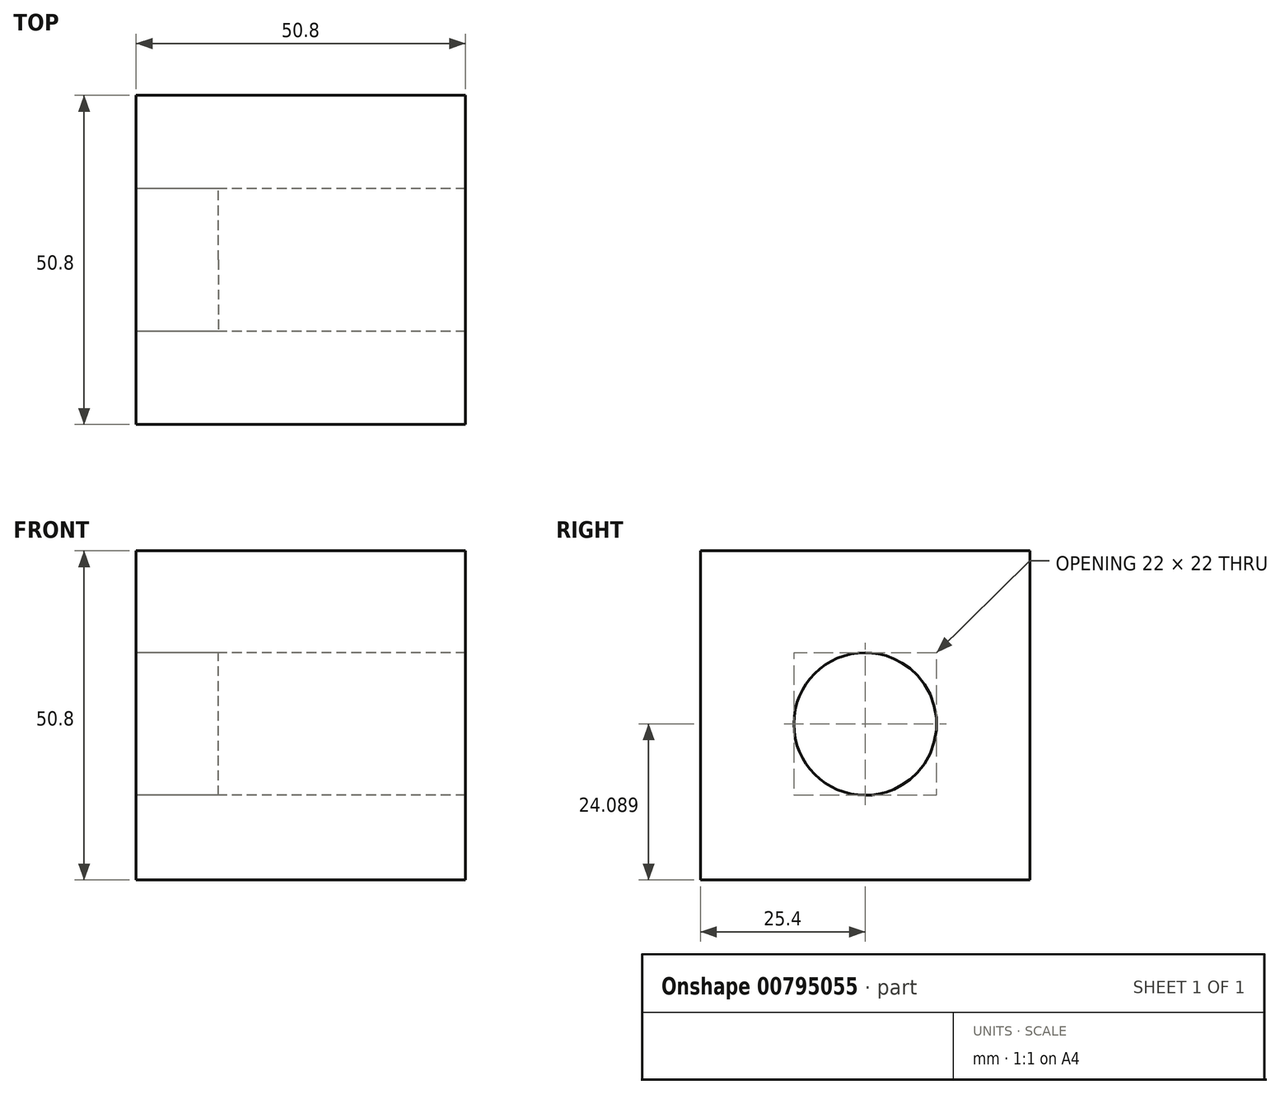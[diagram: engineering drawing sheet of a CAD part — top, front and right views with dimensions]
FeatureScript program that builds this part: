
annotation { "Feature Type Name" : "Feature", "Feature Type Description" : "" }
export const myFeature = defineFeature(function(context is Context, id is Id, definition is map)
    precondition{}
    {
        {
            var Q0;
            Q0=qCreatedBy(makeId("Right.planeOp"),FACE);
            var sketch = newSketch(context, id + "F0", { "sketchPlane" : qUnion([Q0])});
            skLineSegment(sketch, "E0.bottom", {"start": v(0, 50.69) * mm, "end": v(50.8, 50.69) * mm});
            skLineSegment(sketch, "E0.top", {"start": v(0, -0.11) * mm, "end": v(50.8, -0.11) * mm});
            skLineSegment(sketch, "E0.left", {"start": v(0, 50.69) * mm, "end": v(0, -0.11) * mm});
            skLineSegment(sketch, "E0.right", {"start": v(50.8, 50.69) * mm, "end": v(50.8, -0.11) * mm});
            skLineSegment(sketch, "E1", {"start": v(25.4, 50.69) * mm, "end": v(25.4, -0.11) * mm});
            skCircle(sketch, "E2", {"center": v(25.4, 23.98) * mm, "radius": 11 * mm});
            skLineSegment(sketch, "E3", {"start": v(0, 25.29) * mm, "end": v(50.8, 25.29) * mm, "construction": true});
            skSolve(sketch);
        }
        {
            var Q0;
            {var subQ0=sQuery(id+"F0.wireOp",EDGE,"E0.right");Q0=makeQuery(id+"F0.imprint","IMPRINT",FACE,{"disambiguationData":[TD([[makeQuery(id+"F0.imprint","IMPRINT",EDGE,{"derivedFrom":subQ0}),-1.0]])]});}
            var Q1;
            {var subQ5=sQuery(id+"F0.wireOp",EDGE,"E0.left");Q1=makeQuery(id+"F0.imprint","IMPRINT",FACE,{"disambiguationData":[TD([[makeQuery(id+"F0.imprint","IMPRINT",EDGE,{"derivedFrom":subQ5}),1.0]])]});}
            extrude(context, id + "F1", {"entities" : qUnion([Q0, Q1]), "depth" : 50.8 * mm, "offsetDistance" : 25.4 * mm});
        }
        {
            var Q0;
            {var subQ0=sQuery(id+"F0.wireOp",EDGE,"E2");var subQ1=sQuery(id+"F0.wireOp",EDGE,"E1");var subQ2=makeQuery(id+"F0.imprint","INTERSECT",VERTEX,{"disambiguationData":[OD(0.0)],"derivedFrom":[subQ1,subQ0]});Q0=makeQuery(id+"F0.imprint","IMPRINT",FACE,{"disambiguationData":[TD([[makeQuery(id+"F0.imprint","IMPRINT",EDGE,{"disambiguationData":[TD([[subQ2,-1.0]])],"derivedFrom":subQ1}),1.0]])]});}
            var Q1;
            {var subQ0=sQuery(id+"F0.wireOp",EDGE,"E2");var subQ1=sQuery(id+"F0.wireOp",EDGE,"E1");var subQ2=makeQuery(id+"F0.imprint","INTERSECT",VERTEX,{"disambiguationData":[OD(0.0)],"derivedFrom":[subQ1,subQ0]});Q1=makeQuery(id+"F0.imprint","IMPRINT",FACE,{"disambiguationData":[TD([[makeQuery(id+"F0.imprint","IMPRINT",EDGE,{"disambiguationData":[TD([[subQ2,-1.0]])],"derivedFrom":subQ1}),-1.0]])]});}
            extrude(context, id + "F2", {"entities" : qUnion([Q0, Q1]), "depth" : 12.7 * mm, "offsetDistance" : 25.4 * mm});
        }
    });
